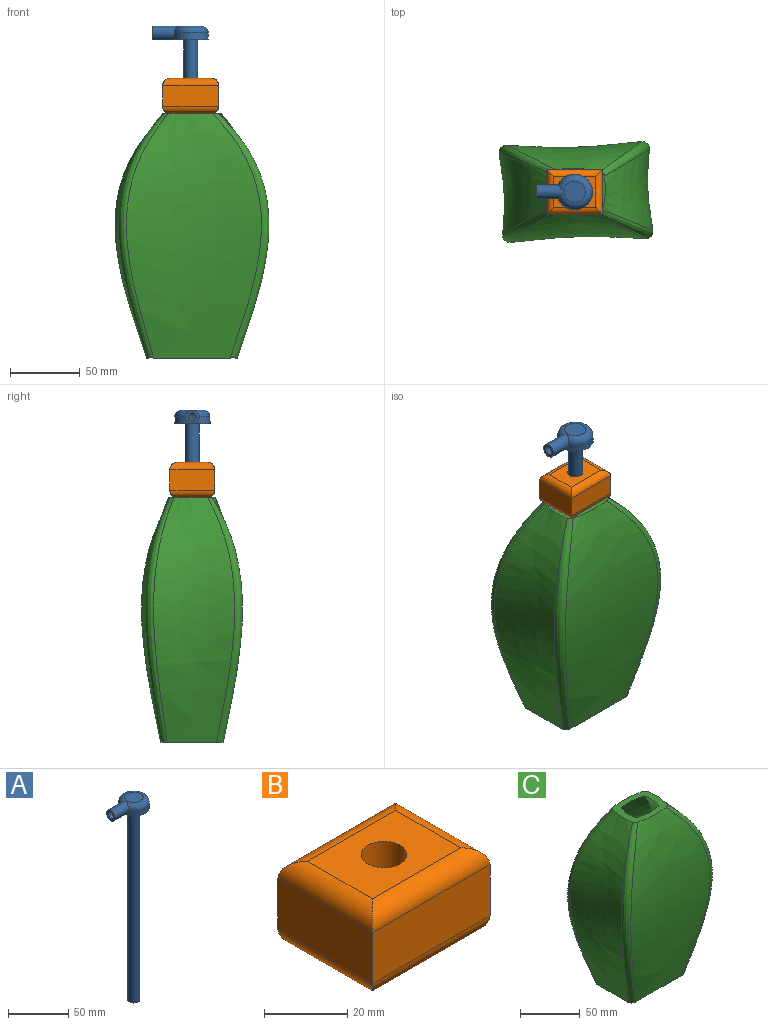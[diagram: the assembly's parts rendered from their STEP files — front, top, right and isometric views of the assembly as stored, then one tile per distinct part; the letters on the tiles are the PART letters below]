
ASSEMBLY  parts=3 mates=2
PART A: 14 faces, bbox 40.6x27.2x205 mm
  f0: plane 15.16x15.16mm, normal (0,0,1), area 180.6mm2, adj f3
  f1: cone r=12.58mm half-angle=3deg, axis (0,0,-1), area 359.8mm2, adj f2,f3,f5
  f2: plane 25.69x25.69mm, normal (0,0,-1), area 439.7mm2, adj f1,f7
  f3: torus R=7.58mm, axis (0,0,-1), area 480.2mm2, adj f0,f1,f5
  f4: plane 10x10mm, normal (-1,0,0), area 50.3mm2, adj f5,f12
  f5: cylinder r=5mm len=19.42mm, axis (1,0,0), area 495.5mm2, adj f1,f3,f4
  f6: plane 10x10mm, normal (0,0,-1), area 50.3mm2, adj f7,f13
  f7: cylinder r=5mm len=195mm, axis (0,0,-1), area 6126.1mm2, adj f2,f6
  f8: plane 15.16x15.16mm, normal (0,0,-1), area 180.6mm2, adj f11
  f9: cone r=10.58mm half-angle=3deg, axis (0,0,-1), area 184.1mm2, adj f10,f11,f12
  f10: plane 21.47x21.47mm, normal (0,0,1), area 333.9mm2, adj f9,f13
  f11: torus R=7.58mm, axis (0,0,-1), area 265.6mm2, adj f8,f9,f12
  f12: cylinder r=3mm len=19.42mm, axis (1,0,0), area 323.2mm2, adj f4,f9,f11
  f13: cylinder r=3mm len=197mm, axis (0,0,-1), area 3713.4mm2, adj f6,f10
PART B: 15 faces, bbox 40x32.1x25 mm
  f0: plane 32.07x15mm, normal (1,0,0), area 481mm2, adj f1,f3,f6,f10
  f1: plane 40x15mm, normal (0,1,0), area 600mm2, adj f0,f2,f7,f11
  f2: plane 32.07x15mm, normal (-1,0,0), area 481mm2, adj f1,f3,f9,f13
  f3: plane 40x15mm, normal (0,-1,0), area 600mm2, adj f0,f2,f8,f12
  f4: plane 30x22.07mm, normal (0,0,1), area 567mm2, adj f10,f11,f12,f13,f14
  f5: plane 30x22.07mm, normal (0,0,-1), area 567mm2, adj f6,f7,f8,f9,f14
  f6: cylinder r=5mm len=32.07mm, axis (0,1,0), area 223.3mm2, adj f0,f5,f7,f8
  f7: cylinder r=5mm len=40mm, axis (-1,0,0), area 285.6mm2, adj f1,f5,f6,f9
  f8: cylinder r=5mm len=40mm, axis (1,0,0), area 285.6mm2, adj f3,f5,f6,f9
  f9: cylinder r=5mm len=32.07mm, axis (0,-1,0), area 223.3mm2, adj f2,f5,f7,f8
  f10: cylinder r=5mm len=32.07mm, axis (0,-1,0), area 223.3mm2, adj f0,f4,f11,f12
  f11: cylinder r=5mm len=40mm, axis (1,0,0), area 285.6mm2, adj f1,f4,f10,f13
  f12: cylinder r=5mm len=40mm, axis (-1,0,0), area 285.6mm2, adj f3,f4,f10,f13
  f13: cylinder r=5mm len=32.07mm, axis (0,1,0), area 223.3mm2, adj f2,f4,f11,f12
  f14: cylinder r=5.5mm len=25mm, axis (0,0,-1), area 863.9mm2, adj f4,f5
PART C: 15 faces, bbox 164.5x109.3x198.4 mm
  f0: offset ~195x158.97mm, area 13371mm2, adj f1,f3,f4,f5
  f1: offset ~195x103.69mm, area 8830.5mm2, adj f0,f2,f4,f5
  f2: offset ~195x158.97mm, area 13371mm2, adj f1,f3,f4,f5
  f3: offset ~195x103.69mm, area 8830.5mm2, adj f0,f2,f4,f5
  f4: plane 58.22x37.2mm, normal (0,0,1), area 2101.2mm2, adj f0,f1,f2,f3
  f5: plane 44.52x35.96mm, normal (0,0,1), area 694.8mm2, adj f0,f1,f2,f3,f7,f8,f9,f10
  f6: plane 65.99x45.99mm, normal (0,0,-1), area 2904.9mm2, adj f7,f8,f9,f10,f11,f12,f13,f14
  f7: bspline ~185x93.69mm, area 8838.4mm2, adj f5,f6,f11,f14
  f8: bspline ~185x148.97mm, area 13550.4mm2, adj f5,f6,f11,f12
  f9: bspline ~185x93.69mm, area 8838.4mm2, adj f5,f6,f12,f13
  f10: bspline ~185x148.97mm, area 13550.4mm2, adj f5,f6,f13,f14
  f11: bspline ~180.7x42.51mm, area 1574.7mm2, adj f5,f6,f7,f8
  f12: bspline ~181.67x37.88mm, area 1546.4mm2, adj f5,f6,f8,f9
  f13: bspline ~180.7x42.51mm, area 1574.7mm2, adj f5,f6,f9,f10
  f14: bspline ~181.67x37.88mm, area 1546.4mm2, adj f5,f6,f7,f10
PLACE A t=(-211.6,72.8,269.73)mm
PLACE B t=(-211.6,72.8,37.23)mm
PLACE C t=(-210.62,73.01,37.23)mm fixed
MATE slider A.f7 <-> B.f14  axis (0,0,-1) through (-211.6,72.8,167.23)mm
MATE fastened C.f5 <-> B.f5  axis (0,0,1) through (-211.6,61.77,212.23)mm
